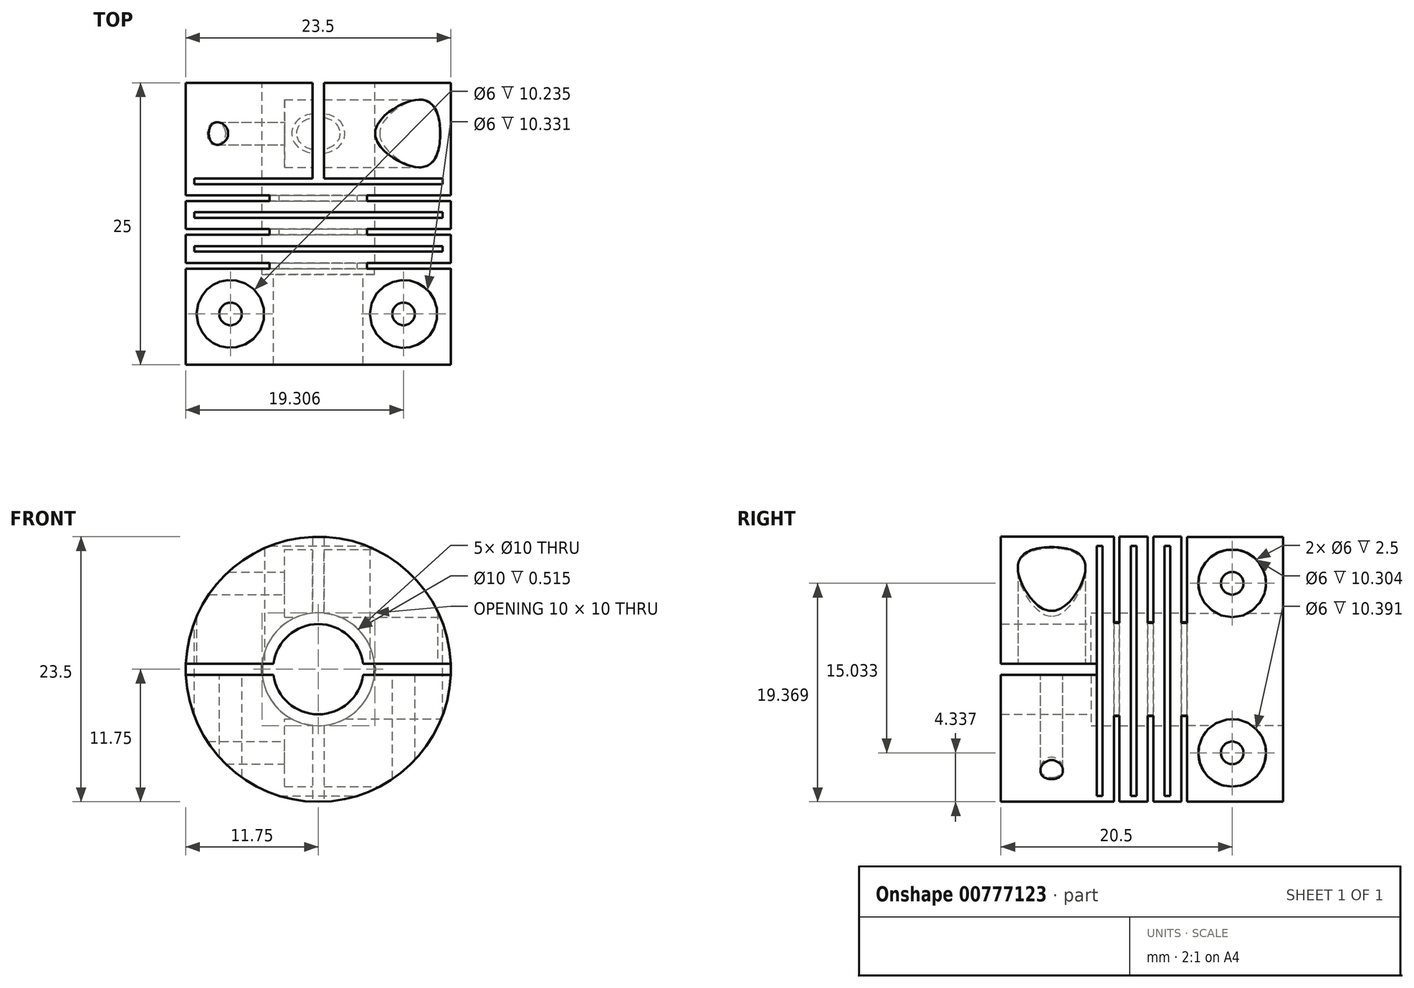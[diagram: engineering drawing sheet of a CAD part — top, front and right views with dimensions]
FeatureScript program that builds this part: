
annotation { "Feature Type Name" : "Feature", "Feature Type Description" : "" }
export const myFeature = defineFeature(function(context is Context, id is Id, definition is map)
    precondition{}
    {
        {
            var Q0;
            Q0=qCreatedBy(makeId("Front.planeOp"),FACE);
            var sketch = newSketch(context, id + "F0", { "sketchPlane" : qUnion([Q0])});
            skCircle(sketch, "E0", {"center": v(0, 0) * mm, "radius": 11.75 * mm});
            skCircle(sketch, "E1", {"center": v(0, 0) * mm, "radius": 4 * mm});
            skCircle(sketch, "E2", {"center": v(0, 0) * mm, "radius": 5 * mm});
            skLineSegment(sketch, "E3.bottom", {"start": v(-0.5, 11.74) * mm, "end": v(0.5, 11.74) * mm});
            skLineSegment(sketch, "E3.top", {"start": v(-0.5, -11.74) * mm, "end": v(0.5, -11.74) * mm});
            skLineSegment(sketch, "E3.left", {"start": v(-0.5, 11.74) * mm, "end": v(-0.5, -11.74) * mm});
            skLineSegment(sketch, "E3.right", {"start": v(0.5, 11.74) * mm, "end": v(0.5, -11.74) * mm});
            skLineSegment(sketch, "E4.bottom", {"start": v(-11.74, 0.5) * mm, "end": v(11.74, 0.5) * mm});
            skLineSegment(sketch, "E4.top", {"start": v(-11.74, -0.5) * mm, "end": v(11.74, -0.5) * mm});
            skLineSegment(sketch, "E4.left", {"start": v(-11.75, 0.5) * mm, "end": v(-11.75, -0.5) * mm});
            skLineSegment(sketch, "E4.right", {"start": v(11.74, 0.5) * mm, "end": v(11.74, -0.5) * mm});
            skSolve(sketch);
        }
        {
            var Q0;
            Q0 = qSketchRegion(id + "F0", true);
            var Q1;
            Q1=makeQuery(id+"F0.imprint","IMPRINT",FACE,{"disambiguationData":[TD([[makeQuery(id+"F0.imprint","IMPRINT",EDGE,{"derivedFrom":sQuery(id+"F0.wireOp",EDGE,"E1")}),-1.0]])]});
            extrude(context, id + "F1", {"entities" : qUnion([Q0, Q1]), "depth" : 25 * mm, "offsetDistance" : 25 * mm});
        }
        {
            var Q0;
            Q0=makeQuery(id+"F0.imprint","IMPRINT",FACE,{"disambiguationData":[TD([[makeQuery(id+"F0.imprint","IMPRINT",EDGE,{"derivedFrom":sQuery(id+"F0.wireOp",EDGE,"E1")}),-1.0]])]});
            extrude(context, id + "F2", {"entities" : qUnion([Q0]), "operationType" : NewBodyOperationType.REMOVE, "depth" : 17 * mm, "offsetDistance" : 25 * mm});
        }
        {
            var Q0;
            {var subQ5=sQuery(id+"F0.wireOp",EDGE,"E3.bottom");Q0=makeQuery(id+"F0.imprint","IMPRINT",FACE,{"disambiguationData":[TD([[makeQuery(id+"F0.imprint","IMPRINT",EDGE,{"derivedFrom":subQ5}),-1.0]])]});}
            var Q1;
            {var subQ5=sQuery(id+"F0.wireOp",EDGE,"E3.top");Q1=makeQuery(id+"F0.imprint","IMPRINT",FACE,{"disambiguationData":[TD([[makeQuery(id+"F0.imprint","IMPRINT",EDGE,{"derivedFrom":subQ5}),1.0]])]});}
            var Q2;
            {var subQ0=sQuery(id+"F0.wireOp",EDGE,"E3.top");Q2=makeQuery(id+"F0.imprint","IMPRINT",FACE,{"disambiguationData":[TD([[makeQuery(id+"F0.imprint","IMPRINT",EDGE,{"derivedFrom":subQ0}),-1.0]])]});}
            var Q3;
            {var subQ0=sQuery(id+"F0.wireOp",EDGE,"E3.bottom");Q3=makeQuery(id+"F0.imprint","IMPRINT",FACE,{"disambiguationData":[TD([[makeQuery(id+"F0.imprint","IMPRINT",EDGE,{"derivedFrom":subQ0}),1.0]])]});}
            extrude(context, id + "F3", {"entities" : qUnion([Q0, Q1, Q2, Q3]), "operationType" : NewBodyOperationType.REMOVE, "depth" : 8.5 * mm, "offsetDistance" : 25 * mm});
        }
        {
            var Q0;
            {var subQ0=sQuery(id+"F0.wireOp",EDGE,"E4.bottom");var subQ1=sQuery(id+"F0.wireOp",EDGE,"E0");var subQ2=makeQuery(id+"F0.imprint","INTERSECT",VERTEX,{"derivedFrom":[subQ1,subQ0]});Q0=makeQuery(id+"F0.imprint","IMPRINT",FACE,{"disambiguationData":[TD([[makeQuery(id+"F0.imprint","IMPRINT",EDGE,{"disambiguationData":[TD([[subQ2,-1.0]])],"derivedFrom":subQ1}),1.0]])]});}
            var Q1;
            {var subQ0=sQuery(id+"F0.wireOp",EDGE,"E4.bottom");var subQ1=sQuery(id+"F0.wireOp",EDGE,"E1");var subQ2=makeQuery(id+"F0.imprint","INTERSECT",VERTEX,{"disambiguationData":[OD(1.0)],"derivedFrom":[subQ1,subQ0]});Q1=makeQuery(id+"F0.imprint","IMPRINT",FACE,{"disambiguationData":[TD([[makeQuery(id+"F0.imprint","IMPRINT",EDGE,{"disambiguationData":[TD([[subQ2,-1.0]])],"derivedFrom":subQ1}),-1.0]])]});}
            var Q2;
            {var subQ0=sQuery(id+"F0.wireOp",EDGE,"E4.bottom");var subQ1=sQuery(id+"F0.wireOp",EDGE,"E1");var subQ2=makeQuery(id+"F0.imprint","INTERSECT",VERTEX,{"disambiguationData":[OD(0.0)],"derivedFrom":[subQ1,subQ0]});Q2=makeQuery(id+"F0.imprint","IMPRINT",FACE,{"disambiguationData":[TD([[makeQuery(id+"F0.imprint","IMPRINT",EDGE,{"disambiguationData":[TD([[subQ2,1.0]])],"derivedFrom":subQ1}),-1.0]])]});}
            var Q3;
            {var subQ5=sQuery(id+"F0.wireOp",EDGE,"E4.right");Q3=makeQuery(id+"F0.imprint","IMPRINT",FACE,{"disambiguationData":[TD([[makeQuery(id+"F0.imprint","IMPRINT",EDGE,{"derivedFrom":subQ5}),-1.0]])]});}
            var Q4;
            {var subQ0=sQuery(id+"F0.wireOp",EDGE,"E4.right");Q4=makeQuery(id+"F0.imprint","IMPRINT",FACE,{"disambiguationData":[TD([[makeQuery(id+"F0.imprint","IMPRINT",EDGE,{"derivedFrom":subQ0}),1.0]])]});}
            extrude(context, id + "F4", {"entities" : qUnion([Q0, Q1, Q2, Q3, Q4]), "operationType" : NewBodyOperationType.REMOVE, "depth" : 25 * mm, "offsetDistance" : 25 * mm, "hasSecondDirection" : true, "secondDirectionOppositeDirection" : false, "secondDirectionDepth" : 16.5 * mm});
        }
        {
            var Q0;
            Q0=qCreatedBy(makeId("Right.planeOp"),FACE);
            var sketch = newSketch(context, id + "F5", { "sketchPlane" : qUnion([Q0])});
            skCircle(sketch, "E5", {"center": v(-4.5, 7.62) * mm, "radius": 3 * mm});
            skCircle(sketch, "E6", {"center": v(-4.5, -7.41) * mm, "radius": 3 * mm});
            skSolve(sketch);
        }
        {
            var Q0;
            Q0 = qSketchRegion(id + "F5", true);
            extrude(context, id + "F6", {"entities" : qUnion([Q0]), "operationType" : NewBodyOperationType.REMOVE, "oppositeDirection" : true, "depth" : 3 * mm, "offsetDistance" : 25 * mm, "hasSecondDirection" : true, "secondDirectionOppositeDirection" : false, "secondDirectionDepth" : 25 * mm});
        }
        {
            var Q0;
            Q0=qCreatedBy(makeId("Top.planeOp"),FACE);
            var sketch = newSketch(context, id + "F7", { "sketchPlane" : qUnion([Q0])});
            skCircle(sketch, "E7", {"center": v(-7.78, -20.5) * mm, "radius": 3 * mm});
            skCircle(sketch, "E8", {"center": v(7.56, -20.5) * mm, "radius": 3 * mm});
            skSolve(sketch);
        }
        {
            var Q0;
            Q0 = qSketchRegion(id + "F7", true);
            extrude(context, id + "F8", {"entities" : qUnion([Q0]), "operationType" : NewBodyOperationType.REMOVE, "depth" : 25 * mm, "offsetDistance" : 25 * mm});
        }
        {
            var Q0;
            Q0=qCreatedBy(makeId("Right.planeOp"),FACE);
            var sketch = newSketch(context, id + "F9", { "sketchPlane" : qUnion([Q0])});
            skLineSegment(sketch, "E9.bottom", {"start": v(-16.49, 10.92) * mm, "end": v(-15.99, 10.92) * mm});
            skLineSegment(sketch, "E9.top", {"start": v(-16.49, -11.23) * mm, "end": v(-15.99, -11.23) * mm});
            skLineSegment(sketch, "E9.left", {"start": v(-16.49, 10.92) * mm, "end": v(-16.49, -11.23) * mm});
            skLineSegment(sketch, "E9.right", {"start": v(-15.99, 10.92) * mm, "end": v(-15.99, -11.23) * mm});
            skLineSegment(sketch, "E10.bottom", {"start": v(-13.49, -11.23) * mm, "end": v(-12.99, -11.23) * mm});
            skLineSegment(sketch, "E10.top", {"start": v(-13.49, 10.92) * mm, "end": v(-12.99, 10.92) * mm});
            skLineSegment(sketch, "E10.left", {"start": v(-13.49, -11.23) * mm, "end": v(-13.49, 10.92) * mm});
            skLineSegment(sketch, "E10.right", {"start": v(-12.99, -11.23) * mm, "end": v(-12.99, 10.92) * mm});
            skLineSegment(sketch, "E11.bottom", {"start": v(-10.49, 10.92) * mm, "end": v(-9.99, 10.92) * mm});
            skLineSegment(sketch, "E11.top", {"start": v(-10.49, -11.23) * mm, "end": v(-9.99, -11.23) * mm});
            skLineSegment(sketch, "E11.left", {"start": v(-10.49, 10.92) * mm, "end": v(-10.49, -11.23) * mm});
            skLineSegment(sketch, "E11.right", {"start": v(-9.99, 10.92) * mm, "end": v(-9.99, -11.23) * mm});
            skSolve(sketch);
        }
        {
            var Q0;
            Q0 = qSketchRegion(id + "F9", true);
            extrude(context, id + "F10", {"entities" : qUnion([Q0]), "operationType" : NewBodyOperationType.REMOVE, "oppositeDirection" : true, "depth" : 25 * mm, "offsetDistance" : 25 * mm, "hasSecondDirection" : true, "secondDirectionOppositeDirection" : false, "secondDirectionDepth" : 25 * mm});
        }
        {
            var Q0;
            Q0=qCreatedBy(makeId("Top.planeOp"),FACE);
            var sketch = newSketch(context, id + "F11", { "sketchPlane" : qUnion([Q0])});
            skLineSegment(sketch, "E12.bottom", {"start": v(-11, -14.49) * mm, "end": v(11, -14.49) * mm});
            skLineSegment(sketch, "E12.top", {"start": v(-11, -14.99) * mm, "end": v(11, -14.99) * mm});
            skLineSegment(sketch, "E12.left", {"start": v(-11, -14.49) * mm, "end": v(-11, -14.99) * mm});
            skLineSegment(sketch, "E12.right", {"start": v(11, -14.49) * mm, "end": v(11, -14.99) * mm});
            skLineSegment(sketch, "E13.bottom", {"start": v(-11, -11.49) * mm, "end": v(11, -11.49) * mm});
            skLineSegment(sketch, "E13.top", {"start": v(-11, -11.99) * mm, "end": v(11, -11.99) * mm});
            skLineSegment(sketch, "E13.left", {"start": v(-11, -11.49) * mm, "end": v(-11, -11.99) * mm});
            skLineSegment(sketch, "E13.right", {"start": v(11, -11.49) * mm, "end": v(11, -11.99) * mm});
            skLineSegment(sketch, "E14.bottom", {"start": v(-11, -8.5) * mm, "end": v(11, -8.5) * mm});
            skLineSegment(sketch, "E14.top", {"start": v(-11, -9) * mm, "end": v(11, -9) * mm});
            skLineSegment(sketch, "E14.left", {"start": v(-11, -8.5) * mm, "end": v(-11, -9) * mm});
            skLineSegment(sketch, "E14.right", {"start": v(11, -8.5) * mm, "end": v(11, -9) * mm});
            skSolve(sketch);
        }
        {
            var Q0;
            Q0 = qSketchRegion(id + "F11", true);
            extrude(context, id + "F12", {"entities" : qUnion([Q0]), "operationType" : NewBodyOperationType.REMOVE, "oppositeDirection" : true, "depth" : 25 * mm, "offsetDistance" : 25 * mm, "hasSecondDirection" : true, "secondDirectionOppositeDirection" : false, "secondDirectionDepth" : 25 * mm});
        }
        {
            var Q0;
            Q0=makeQuery(id+"F6.boolean.opBoolean","COPY",FACE,{"derivedFrom":makeQuery(id+"F6.opExtrude","CAP_FACE",FACE,{"disambiguationData":[OSD([sQuery(id+"F5.wireOp",EDGE,"E6")])],"isStart":false})});
            var sketch = newSketch(context, id + "F13", { "sketchPlane" : qUnion([Q0])});
            skCircle(sketch, "E15", {"center": v(-4.5, -7.41) * mm, "radius": 1 * mm});
            skCircle(sketch, "E16", {"center": v(-4.5, 7.62) * mm, "radius": 1 * mm});
            skSolve(sketch);
        }
        {
            var Q0;
            Q0=makeQuery(id+"F13.imprint","IMPRINT",FACE,{"disambiguationData":[TD([[makeQuery(id+"F13.imprint","IMPRINT",EDGE,{"derivedFrom":sQuery(id+"F13.wireOp",EDGE,"E15")}),1.0]])]});
            var Q1;
            Q1=makeQuery(id+"F13.imprint","IMPRINT",FACE,{"disambiguationData":[TD([[makeQuery(id+"F13.imprint","IMPRINT",EDGE,{"derivedFrom":sQuery(id+"F13.wireOp",EDGE,"E16")}),1.0]])]});
            extrude(context, id + "F14", {"entities" : qUnion([Q0, Q1]), "operationType" : NewBodyOperationType.REMOVE, "oppositeDirection" : true, "depth" : 25 * mm, "offsetDistance" : 25 * mm});
        }
        {
            var Q0;
            {var subQ0=sQuery(id+"F0.wireOp",EDGE,"E4.top");Q0=makeQuery(id+"F4.boolean.opBoolean","COPY",FACE,{"derivedFrom":makeQuery(id+"F4.opExtrude","SWEPT_FACE",FACE,{"disambiguationData":[OSD([subQ0]),TDD([makeQuery(id+"F0.imprint","IMPRINT",EDGE,{"disambiguationData":[TD([[makeQuery(id+"F0.imprint","INTERSECT",VERTEX,{"derivedFrom":[sQuery(id+"F0.wireOp",EDGE,"E0"),subQ0]}),-1.0]])],"derivedFrom":subQ0}),makeQuery(id+"F0.imprint","IMPRINT",EDGE,{"disambiguationData":[TD([[makeQuery(id+"F0.imprint","INTERSECT",VERTEX,{"disambiguationData":[OD(0.0)],"derivedFrom":[sQuery(id+"F0.wireOp",EDGE,"E1"),subQ0]}),1.0]])],"derivedFrom":subQ0})])]})});}
            var sketch = newSketch(context, id + "F15", { "sketchPlane" : qUnion([Q0])});
            skCircle(sketch, "E17", {"center": v(-7.78, -20.5) * mm, "radius": 1 * mm});
            skCircle(sketch, "E18", {"center": v(7.56, -20.5) * mm, "radius": 1 * mm});
            skSolve(sketch);
        }
        {
            var Q0;
            Q0=makeQuery(id+"F15.imprint","IMPRINT",FACE,{"disambiguationData":[TD([[makeQuery(id+"F15.imprint","IMPRINT",EDGE,{"derivedFrom":sQuery(id+"F15.wireOp",EDGE,"E18")}),1.0]])]});
            var Q1;
            Q1=makeQuery(id+"F15.imprint","IMPRINT",FACE,{"disambiguationData":[TD([[makeQuery(id+"F15.imprint","IMPRINT",EDGE,{"derivedFrom":sQuery(id+"F15.wireOp",EDGE,"E17")}),1.0]])]});
            extrude(context, id + "F16", {"entities" : qUnion([Q0, Q1]), "operationType" : NewBodyOperationType.REMOVE, "oppositeDirection" : true, "depth" : 25 * mm, "offsetDistance" : 25 * mm});
        }
    });
